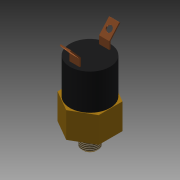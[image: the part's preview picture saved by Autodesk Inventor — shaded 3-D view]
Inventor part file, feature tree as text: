
AUTODESK INVENTOR PART (.ipt)
format: ipt  version: 2016 SP1 (Build 200210100, 210)  size: 162,304 bytes
history: native  units: mm (DEFAULTED — no unit token found)
features: extrude x6, sketch x6, projected_geometry x4, mirror x1, thread x1, chamfer x1, fillet x1
ambient origin geometry x8: Origin, YZ Plane, XZ Plane, XY Plane, X Axis, Y Axis, Z Axis, Center Point
bodies: Solid1 (feature_tree)
feature tree (20):
  extrude  "Extrusion1"  Depth=15.875mm TaperAngle=0.0deg
  extrude  "Extrusion2"  Depth=11.049mm TaperAngle=0.0deg
  extrude  "Extrusion3"  Depth=19.9898mm TaperAngle=0.0deg
  extrude  "Extrusion4"  Depth=21.971mm TaperAngle=0.0deg
  extrude  "Extrusion5"  Depth=0.762mm
  extrude  "Extrusion6"  Depth=3.175mm
  mirror  "Mirror1"
  thread  "Thread1"  [1 undecoded]
  chamfer  "Chamfer1"  Distance=6.35mm
  fillet  "Fillet1"  Radius=6.35mm
  sketch  "Sketch1"  dims[d0=25.4mm d1=15.875mm d2=0.0mm]
  sketch  "Sketch2"  dims[d3=10.16mm d4=11.049mm d5=0.0mm]
  projected_geometry  "Projected Loop1"
  sketch  "Sketch3"  dims[d6=3.175mm d7=19.9898mm d8=0.0mm]
  sketch  "Sketch4"  dims[d9=24.765mm d10=21.971mm d11=0.0mm]
  projected_geometry  "Projected Loop2"
  sketch  "Sketch5"  dims[d12=19.05mm d13=0.762mm]
  projected_geometry  "Projected Loop3"
  sketch  "Sketch6"  dims[d14=0.762mm d15=4.699mm d17=9.398mm d18=6.35mm d19=0.0mm d20=6.35mm d21=0.0mm d22=25.4mm d23=0.0mm d24=1.0mm d25=3.175mm d26=45.0deg d27=3.175mm]
  projected_geometry  "Projected Loop4"
note: 1 required parameter value undecoded (feature->parameter linkage not recoverable at this tier; creation-order binding heuristic only, values carry confidence <= 0.55)
